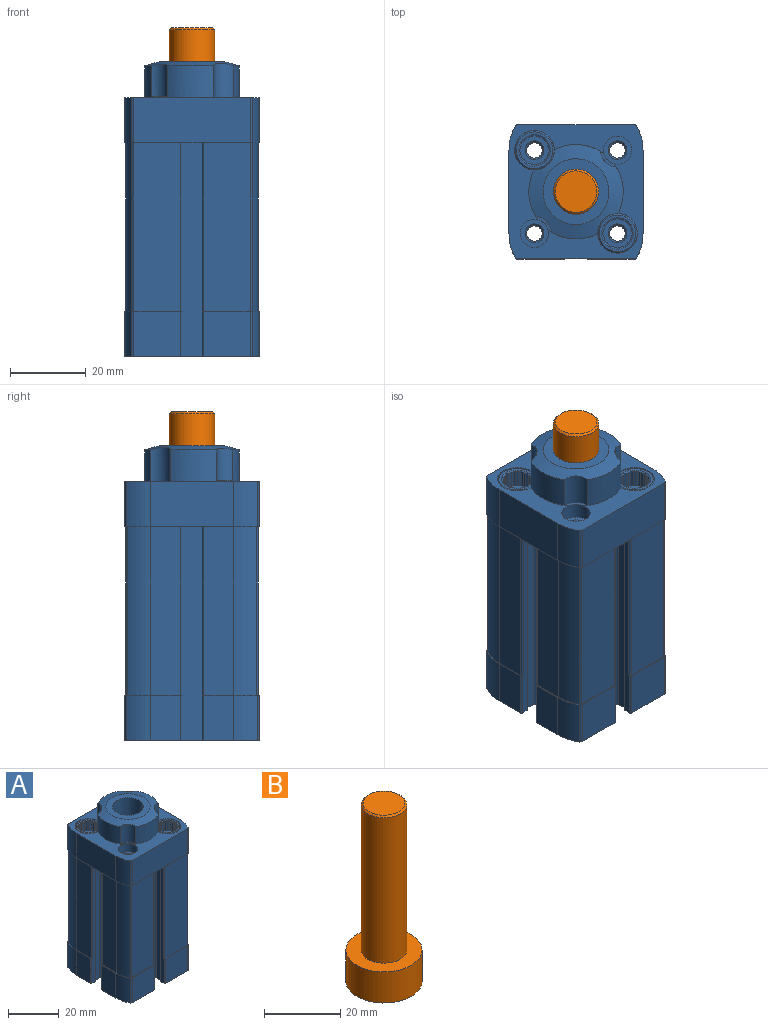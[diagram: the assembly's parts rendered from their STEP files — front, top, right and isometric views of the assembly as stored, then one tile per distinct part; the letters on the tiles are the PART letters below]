
ASSEMBLY  parts=2 mates=1
PART A: 305 faces, bbox 35.5x35.5x78 mm
  f0: cylinder r=4.5mm len=8.67mm, axis (0,0,-1), area 54.5mm2, adj f1,f4,f93,f202
  f1: cylinder r=12.5mm len=13.11mm, axis (0,0,1), area 107.9mm2, adj f0,f93,f186,f196,f201,f202
  f2: cylinder r=12.5mm len=13.11mm, axis (0,0,1), area 107.9mm2, adj f194,f195,f196,f201,f202,f293
  f3: cylinder r=3.75mm len=4.54mm, axis (0,0,1), area 3.6mm2, adj f11,f12,f192,f286
  f4: cylinder r=12.5mm len=13.11mm, axis (0,0,1), area 107.9mm2, adj f0,f93,f179,f186,f201,f202
  f5: cylinder r=3.75mm len=4.54mm, axis (0,0,1), area 3.6mm2, adj f8,f64,f225,f298
  f6: cylinder r=3.75mm len=4.54mm, axis (0,0,1), area 3.6mm2, adj f8,f80,f81,f298
  f7: cylinder r=3.75mm len=4.54mm, axis (0,0,1), area 3.6mm2, adj f8,f65,f66,f298
  f8: cone r=866.03mm half-angle=60deg, axis (0,0,-1), area 10.5mm2, adj f5,f6,f7,f9,f64,f65,f66,f67
  f9: cylinder r=3.75mm len=4.54mm, axis (0,0,1), area 3.6mm2, adj f8,f67,f220,f298
  f10: plane 4.75x0.71mm, normal (1,0,0), area 3.1mm2, adj f11,f192,f217,f286
  f11: plane 4.74x0.62mm, normal (0.5,-0.87,0), area 3.1mm2, adj f3,f10,f192,f286
  f12: plane 4.74x0.62mm, normal (0.87,-0.5,0), area 3.1mm2, adj f3,f192,f250,f286
  f13: plane 4.74x0.62mm, normal (0.5,-0.87,0), area 3.1mm2, adj f14,f192,f285,f286
  f14: plane 4.74x0.62mm, normal (-0.5,-0.87,0), area 3.1mm2, adj f13,f192,f193,f286
  f15: plane 4.75x0.71mm, normal (0,-1,0), area 3.1mm2, adj f192,f193,f249,f286
  f16: plane 4.74x0.62mm, normal (-0.5,-0.87,0), area 3.1mm2, adj f17,f192,f278,f286
  f17: plane 4.75x0.71mm, normal (-1,0,0), area 3.1mm2, adj f16,f192,f277,f286
  f18: plane 4.74x0.62mm, normal (-0.87,-0.5,0), area 3.1mm2, adj f192,f248,f277,f286
  f19: plane 4.74x0.71mm, normal (-1,0,0), area 3.1mm2, adj f20,f192,f279,f286
  f20: plane 4.74x0.62mm, normal (-0.5,0.87,0), area 3.1mm2, adj f19,f192,f280,f286
  f21: plane 4.74x0.62mm, normal (-0.87,0.5,0), area 3.1mm2, adj f192,f247,f280,f286
  f22: plane 4.74x0.62mm, normal (-0.5,0.87,0), area 3.1mm2, adj f23,f192,f284,f286
  f23: plane 4.74x0.62mm, normal (0.5,0.87,0), area 3.1mm2, adj f22,f192,f283,f286
  f24: plane 4.74x0.71mm, normal (0,1,0), area 3.1mm2, adj f192,f246,f283,f286
  f25: plane 4.74x0.62mm, normal (0.5,0.87,0), area 3.1mm2, adj f26,f192,f282,f286
  f26: plane 4.74x0.71mm, normal (1,0,0), area 3.1mm2, adj f25,f192,f281,f286
  f27: plane 4.74x0.62mm, normal (0.87,0.5,0), area 3.1mm2, adj f192,f245,f281,f286
  f28: plane 4.75x0.71mm, normal (1,0,0), area 3.1mm2, adj f29,f198,f215,f254
  f29: plane 4.74x0.62mm, normal (0.5,-0.87,0), area 3.1mm2, adj f28,f198,f216,f254
  f30: plane 4.74x0.62mm, normal (0.87,-0.5,0), area 3.1mm2, adj f198,f216,f244,f254
  f31: plane 4.74x0.62mm, normal (0.5,-0.87,0), area 3.1mm2, adj f32,f198,f218,f254
  f32: plane 4.74x0.62mm, normal (-0.5,-0.87,0), area 3.1mm2, adj f31,f198,f214,f254
  f33: plane 4.75x0.71mm, normal (0,-1,0), area 3.1mm2, adj f198,f214,f243,f254
  f34: plane 4.74x0.62mm, normal (-0.5,-0.87,0), area 3.1mm2, adj f35,f198,f254,f275
  f35: plane 4.75x0.71mm, normal (-1,0,0), area 3.1mm2, adj f34,f198,f254,f274
  f36: plane 4.74x0.62mm, normal (-0.87,-0.5,0), area 3.1mm2, adj f198,f242,f254,f274
  f37: plane 4.74x0.71mm, normal (-1,0,0), area 3.1mm2, adj f38,f198,f254,f273
  f38: plane 4.74x0.62mm, normal (-0.5,0.87,0), area 3.1mm2, adj f37,f198,f254,f272
  f39: plane 4.74x0.62mm, normal (-0.87,0.5,0), area 3.1mm2, adj f198,f241,f254,f272
  f40: plane 4.74x0.62mm, normal (-0.5,0.87,0), area 3.1mm2, adj f41,f198,f254,f271
  f41: plane 4.74x0.62mm, normal (0.5,0.87,0), area 3.1mm2, adj f40,f198,f254,f270
  f42: plane 4.74x0.71mm, normal (0,1,0), area 3.1mm2, adj f198,f240,f254,f270
  f43: plane 4.74x0.62mm, normal (0.5,0.87,0), area 3.1mm2, adj f44,f198,f254,f269
  f44: plane 4.74x0.71mm, normal (1,0,0), area 3.1mm2, adj f43,f198,f254,f268
  f45: plane 4.74x0.62mm, normal (0.87,0.5,0), area 3.1mm2, adj f198,f239,f254,f268
  f46: plane 4.75x0.71mm, normal (1,0,0), area 3.1mm2, adj f47,f180,f181,f256
  f47: plane 4.74x0.62mm, normal (0.5,-0.87,0), area 3.1mm2, adj f46,f181,f256,f257
  f48: plane 4.74x0.62mm, normal (0.87,-0.5,0), area 3.1mm2, adj f181,f238,f256,f257
  f49: plane 4.74x0.62mm, normal (0.5,-0.87,0), area 3.1mm2, adj f50,f181,f256,f258
  f50: plane 4.74x0.62mm, normal (-0.5,-0.87,0), area 3.1mm2, adj f49,f181,f256,f259
  f51: plane 4.75x0.71mm, normal (0,-1,0), area 3.1mm2, adj f181,f237,f256,f259
  f52: plane 4.74x0.62mm, normal (-0.5,-0.87,0), area 3.1mm2, adj f53,f181,f256,f260
  f53: plane 4.75x0.71mm, normal (-1,0,0), area 3.1mm2, adj f52,f181,f256,f261
  f54: plane 4.74x0.62mm, normal (-0.87,-0.5,0), area 3.1mm2, adj f181,f236,f256,f261
  f55: plane 4.74x0.71mm, normal (-1,0,0), area 3.1mm2, adj f56,f181,f256,f262
  f56: plane 4.74x0.62mm, normal (-0.5,0.87,0), area 3.1mm2, adj f55,f181,f256,f263
  f57: plane 4.74x0.62mm, normal (-0.87,0.5,0), area 3.1mm2, adj f181,f235,f256,f263
  f58: plane 4.74x0.62mm, normal (-0.5,0.87,0), area 3.1mm2, adj f59,f181,f256,f264
  f59: plane 4.74x0.62mm, normal (0.5,0.87,0), area 3.1mm2, adj f58,f181,f256,f265
  f60: plane 4.74x0.71mm, normal (0,1,0), area 3.1mm2, adj f181,f234,f256,f265
  f61: plane 4.74x0.62mm, normal (0.5,0.87,0), area 3.1mm2, adj f62,f181,f256,f266
  f62: plane 4.74x0.71mm, normal (1,0,0), area 3.1mm2, adj f61,f181,f256,f267
  f63: plane 4.74x0.62mm, normal (0.87,0.5,0), area 3.1mm2, adj f181,f219,f256,f267
  f64: plane 4.75x0.71mm, normal (1,0,0), area 3.1mm2, adj f5,f8,f65,f298
  f65: plane 4.74x0.62mm, normal (0.5,-0.87,0), area 3.1mm2, adj f7,f8,f64,f298
  f66: plane 4.74x0.62mm, normal (0.87,-0.5,0), area 3.1mm2, adj f7,f8,f220,f298
  f67: plane 4.74x0.62mm, normal (0.5,-0.87,0), area 3.1mm2, adj f8,f9,f68,f298
  f68: plane 4.74x0.62mm, normal (-0.5,-0.87,0), area 3.1mm2, adj f8,f67,f233,f298
  f69: plane 4.75x0.71mm, normal (0,-1,0), area 3.1mm2, adj f8,f221,f233,f298
  f70: plane 4.74x0.62mm, normal (-0.5,-0.87,0), area 3.1mm2, adj f8,f71,f232,f298
  f71: plane 4.75x0.71mm, normal (-1,0,0), area 3.1mm2, adj f8,f70,f231,f298
  f72: plane 4.74x0.62mm, normal (-0.87,-0.5,0), area 3.1mm2, adj f8,f222,f231,f298
  f73: plane 4.74x0.71mm, normal (-1,0,0), area 3.1mm2, adj f8,f74,f230,f298
  f74: plane 4.74x0.62mm, normal (-0.5,0.87,0), area 3.1mm2, adj f8,f73,f229,f298
  f75: plane 4.74x0.62mm, normal (-0.87,0.5,0), area 3.1mm2, adj f8,f223,f229,f298
  f76: plane 4.74x0.62mm, normal (-0.5,0.87,0), area 3.1mm2, adj f8,f77,f227,f298
  f77: plane 4.74x0.62mm, normal (0.5,0.87,0), area 3.1mm2, adj f8,f76,f226,f298
  f78: plane 4.74x0.71mm, normal (0,1,0), area 3.1mm2, adj f8,f224,f226,f298
  f79: plane 4.74x0.62mm, normal (0.5,0.87,0), area 3.1mm2, adj f8,f80,f228,f298
  f80: plane 4.74x0.71mm, normal (1,0,0), area 3.1mm2, adj f6,f8,f79,f298
  f81: plane 4.74x0.62mm, normal (0.87,0.5,0), area 3.1mm2, adj f6,f8,f225,f298
  f82: plane 4.13x4.13mm, normal (0,1,0), area 13.4mm2, adj f83
  f83: cylinder r=2.07mm len=6.57mm, axis (0,1,0), area 85.3mm2, adj f82,f84
  f84: cone r=2.5mm half-angle=45deg, axis (0,1,0), area 8.8mm2, adj f83,f204
  f85: plane 4.13x4.13mm, normal (0,1,0), area 13.4mm2, adj f86
  f86: cylinder r=2.07mm len=5.57mm, axis (0,1,0), area 72.3mm2, adj f85,f87
  f87: cone r=2.5mm half-angle=45deg, axis (0,1,0), area 8.8mm2, adj f86,f164
  f88: plane 20x20mm, normal (0,0,1), area 314.2mm2, adj f89
  f89: cylinder r=10mm len=25mm, axis (0,0,1), area 1570.8mm2, adj f88,f90
  f90: plane 20x20mm, normal (0,0,-1), area 201.1mm2, adj f89,f91
  f91: cylinder r=6mm len=31.25mm, axis (0,0,1), area 1178.1mm2, adj f90,f92
  f92: plane 17.45x17.45mm, normal (0,0,1), area 126mm2, adj f91,f202
  f93: plane 4.16x4.16mm, normal (0,0,1), area 4mm2, adj f0,f1,f4,f186
  f94: plane 9x9mm, normal (0,0,-1), area 63.6mm2, adj f95
  f95: cylinder r=4.5mm len=9mm, axis (0,0,1), area 59.4mm2, adj f94,f161
  f96: cylinder r=0.4mm len=12mm, axis (0,0,-1), area 7.5mm2, adj f103,f147,f161,f206
  f97: cylinder r=0.4mm len=12mm, axis (0,0,-1), area 7.5mm2, adj f115,f161,f208,f299
  f98: cylinder r=0.4mm len=12mm, axis (0,0,-1), area 7.5mm2, adj f118,f161,f210,f299
  f99: cylinder r=0.4mm len=12mm, axis (0,0,-1), area 7.5mm2, adj f130,f161,f209,f300
  f100: cylinder r=0.4mm len=12mm, axis (0,0,-1), area 7.5mm2, adj f133,f161,f176,f300
  f101: cylinder r=0.4mm len=12mm, axis (0,0,-1), area 7.5mm2, adj f145,f147,f161,f175
  f102: cylinder r=0.4mm len=44.5mm, axis (0,0,-1), area 28mm2, adj f103,f147,f148,f154
  f103: plane 56.5x1.85mm, normal (0,-1,0), area 93.4mm2, adj f96,f102,f104,f147,f148,f161
  f104: cylinder r=0.2mm len=56.5mm, axis (0,0,-1), area 17.7mm2, adj f103,f105,f148,f161
  f105: plane 56.5x0.2mm, normal (-1,0,0), area 11.3mm2, adj f104,f106,f148,f161
  f106: cylinder r=0.3mm len=56.5mm, axis (0,0,-1), area 26.6mm2, adj f105,f107,f148,f161
  f107: plane 56.5x2.5mm, normal (0,-1,0), area 141.2mm2, adj f106,f108,f148,f161
  f108: cylinder r=0.6mm len=56.5mm, axis (0,0,-1), area 53.2mm2, adj f107,f109,f148,f161
  f109: plane 56.5x5.6mm, normal (1,0,0), area 316.4mm2, adj f108,f110,f148,f161
  f110: cylinder r=0.6mm len=56.5mm, axis (0,0,-1), area 53.2mm2, adj f109,f111,f148,f161
  f111: plane 56.5x2.5mm, normal (0,1,0), area 141.2mm2, adj f110,f112,f148,f161
  f112: cylinder r=0.3mm len=56.5mm, axis (0,0,-1), area 26.6mm2, adj f111,f113,f148,f161
  f113: plane 56.5x0.2mm, normal (-1,0,0), area 11.3mm2, adj f112,f114,f148,f161
  f114: cylinder r=0.2mm len=56.5mm, axis (0,0,-1), area 17.7mm2, adj f113,f115,f148,f161
  f115: plane 56.5x1.85mm, normal (0,1,0), area 93.4mm2, adj f97,f114,f116,f148,f161,f299
  f116: cylinder r=0.4mm len=44.5mm, axis (0,0,-1), area 28mm2, adj f115,f148,f299,f301
  f117: cylinder r=0.4mm len=44.5mm, axis (0,0,-1), area 28mm2, adj f118,f148,f157,f299
  f118: plane 56.5x1.85mm, normal (-1,0,0), area 93.4mm2, adj f98,f117,f119,f148,f161,f299
  f119: cylinder r=0.2mm len=56.5mm, axis (0,0,-1), area 17.7mm2, adj f118,f120,f148,f161
  f120: plane 56.5x0.2mm, normal (0,1,0), area 11.3mm2, adj f119,f121,f148,f161
  f121: cylinder r=0.3mm len=56.5mm, axis (0,0,-1), area 26.6mm2, adj f120,f122,f148,f161
  f122: plane 56.5x2.5mm, normal (-1,0,0), area 141.2mm2, adj f121,f123,f148,f161
  f123: cylinder r=0.6mm len=56.5mm, axis (0,0,-1), area 53.2mm2, adj f122,f124,f148,f161
  f124: plane 56.5x5.6mm, normal (0,-1,0), area 316.4mm2, adj f123,f125,f148,f161
  f125: cylinder r=0.6mm len=56.5mm, axis (0,0,-1), area 53.2mm2, adj f124,f126,f148,f161
  f126: plane 56.5x2.5mm, normal (1,0,0), area 141.2mm2, adj f125,f127,f148,f161
  f127: cylinder r=0.3mm len=56.5mm, axis (0,0,-1), area 26.6mm2, adj f126,f128,f148,f161
  f128: plane 56.5x0.2mm, normal (0,1,0), area 11.3mm2, adj f127,f129,f148,f161
  f129: cylinder r=0.2mm len=56.5mm, axis (0,0,-1), area 17.7mm2, adj f128,f130,f148,f161
  f130: plane 56.5x1.85mm, normal (1,0,0), area 93.4mm2, adj f99,f129,f131,f148,f161,f300
  f131: cylinder r=0.4mm len=44.5mm, axis (0,0,-1), area 28mm2, adj f130,f148,f300,f302
  f132: cylinder r=0.4mm len=44.5mm, axis (0,0,-1), area 28mm2, adj f133,f148,f160,f300
  f133: plane 56.5x1.85mm, normal (0,1,0), area 93.4mm2, adj f100,f132,f134,f148,f161,f300
  f134: cylinder r=0.2mm len=56.5mm, axis (0,0,-1), area 17.7mm2, adj f133,f135,f148,f161
  f135: plane 56.5x0.2mm, normal (1,0,0), area 11.3mm2, adj f134,f136,f148,f161
  f136: cylinder r=0.3mm len=56.5mm, axis (0,0,-1), area 26.6mm2, adj f135,f137,f148,f161
  f137: plane 56.5x2.5mm, normal (0,1,0), area 141.2mm2, adj f136,f138,f148,f161
  f138: cylinder r=0.6mm len=56.5mm, axis (0,0,-1), area 53.2mm2, adj f137,f139,f148,f161
  f139: plane 56.5x5.6mm, normal (-1,0,0), area 316.4mm2, adj f138,f140,f148,f161
  f140: cylinder r=0.6mm len=56.5mm, axis (0,0,-1), area 53.2mm2, adj f139,f141,f148,f161
  f141: plane 56.5x2.5mm, normal (0,-1,0), area 141.2mm2, adj f140,f142,f148,f161
  f142: cylinder r=0.3mm len=56.5mm, axis (0,0,-1), area 26.6mm2, adj f141,f143,f148,f161
  f143: plane 56.5x0.2mm, normal (1,0,0), area 11.3mm2, adj f142,f144,f148,f161
  f144: cylinder r=0.2mm len=56.5mm, axis (0,0,-1), area 17.7mm2, adj f143,f145,f148,f161
  f145: plane 56.5x1.85mm, normal (0,-1,0), area 93.4mm2, adj f101,f144,f146,f147,f148,f161
  f146: cylinder r=0.4mm len=44.5mm, axis (0,0,-1), area 28mm2, adj f145,f147,f148,f303
  f147: plane 35.5x15.05mm, normal (0,0,1), area 15.5mm2, adj f96,f101,f102,f103,f145,f146,f149,f150
  f148: plane 35.5x35.5mm, normal (0,0,-1), area 138.3mm2, adj f102,f103,f104,f105,f106,f107,f108,f109
  f149: cylinder r=12.75mm len=44.5mm, axis (0,0,-1), area 287.7mm2, adj f147,f148,f150,f303
  f150: cylinder r=0.6mm len=44.5mm, axis (0,0,-1), area 28.4mm2, adj f147,f148,f149,f151
  f151: plane 44.5x30.74mm, normal (0,1,0), area 1368mm2, adj f147,f148,f150,f152
  f152: cylinder r=0.6mm len=44.5mm, axis (0,0,-1), area 28.4mm2, adj f147,f148,f151,f153
  f153: cylinder r=12.75mm len=44.5mm, axis (0,0,-1), area 287.7mm2, adj f147,f148,f152,f154
  f154: plane 44.5x7.9mm, normal (1,0,0), area 351.5mm2, adj f102,f147,f148,f153
  f155: cylinder r=12.75mm len=44.5mm, axis (0,0,-1), area 287.7mm2, adj f148,f156,f299,f301
  f156: cylinder r=0.6mm len=44.5mm, axis (0,0,-1), area 28.4mm2, adj f148,f155,f157,f299
  f157: plane 44.5x12.27mm, normal (0,-1,0), area 546.1mm2, adj f117,f148,f156,f299
  f158: cylinder r=0.6mm len=44.5mm, axis (0,0,-1), area 28.4mm2, adj f148,f159,f300,f302
  f159: cylinder r=12.75mm len=44.5mm, axis (0,0,-1), area 287.7mm2, adj f148,f158,f160,f300
  f160: plane 44.5x7.9mm, normal (-1,0,0), area 351.5mm2, adj f132,f148,f159,f300
  f161: plane 35.5x35.5mm, normal (0,0,-1), area 770.9mm2, adj f95,f96,f97,f98,f99,f100,f101,f103
  f162: plane 9.7x9.7mm, normal (0,0,1), area 18.5mm2, adj f286,f287
  f163: cylinder r=0.85mm len=12mm, axis (0,0,-1), area 10.9mm2, adj f148,f164,f174,f201
  f164: plane 30.74x12mm, normal (0,1,0), area 349.3mm2, adj f87,f148,f163,f165,f201
  f165: cylinder r=0.85mm len=12mm, axis (0,0,-1), area 10.9mm2, adj f148,f164,f166,f201
  f166: cylinder r=13mm len=12mm, axis (0,0,-1), area 79.1mm2, adj f148,f165,f167,f201
  f167: plane 22x12mm, normal (1,0,0), area 264mm2, adj f148,f166,f168,f201
  f168: cylinder r=13mm len=12mm, axis (0,0,-1), area 79.1mm2, adj f148,f167,f169,f201
  f169: cylinder r=0.85mm len=12mm, axis (0,0,-1), area 10.9mm2, adj f148,f168,f170,f201
  f170: plane 30.74x12mm, normal (0,-1,0), area 368.9mm2, adj f148,f169,f171,f201
  f171: cylinder r=0.85mm len=12mm, axis (0,0,-1), area 10.9mm2, adj f148,f170,f172,f201
  f172: cylinder r=13mm len=12mm, axis (0,0,-1), area 79.1mm2, adj f148,f171,f173,f201
  f173: plane 22x12mm, normal (-1,0,0), area 264mm2, adj f148,f172,f174,f201
  f174: cylinder r=13mm len=12mm, axis (0,0,-1), area 79.1mm2, adj f148,f163,f173,f201
  f175: plane 12x7.9mm, normal (-1,0,0), area 94.8mm2, adj f101,f147,f161,f178
  f176: plane 12x7.9mm, normal (-1,0,0), area 94.8mm2, adj f100,f161,f177,f300
  f177: cylinder r=13mm len=12mm, axis (0,0,-1), area 79.1mm2, adj f161,f176,f212,f300
  f178: cylinder r=13mm len=12mm, axis (0,0,-1), area 79.1mm2, adj f147,f161,f175,f304
  f179: cylinder r=5.25mm len=10.5mm, axis (0,0,1), area 88mm2, adj f4,f201,f202,f213,f287
  f180: cylinder r=3.75mm len=4.54mm, axis (0,0,1), area 3.6mm2, adj f46,f181,f219,f256
  f181: plane 8.08x8.08mm, normal (0,0,-1), area 26.5mm2, adj f46,f47,f48,f49,f50,f51,f52,f53
  f182: cone r=2.07mm half-angle=45deg, axis (0,0,-1), area 8.8mm2, adj f181,f183
  f183: cylinder r=2.07mm len=58.83mm, axis (0,0,1), area 764.1mm2, adj f182,f184
  f184: cone r=2.5mm half-angle=45deg, axis (0,0,1), area 8.8mm2, adj f183,f185
  f185: plane 7.5x7.5mm, normal (0,0,1), area 24.5mm2, adj f184,f186
  f186: cylinder r=3.75mm len=7.5mm, axis (0,0,1), area 95.1mm2, adj f1,f4,f93,f185,f201
  f187: cylinder r=4.5mm len=9mm, axis (0,0,1), area 135.7mm2, adj f161,f188
  f188: plane 9x9mm, normal (0,0,-1), area 44mm2, adj f187,f189
  f189: cone r=2.07mm half-angle=45deg, axis (0,0,-1), area 8.8mm2, adj f188,f190
  f190: cylinder r=2.07mm len=58.03mm, axis (0,0,1), area 753.7mm2, adj f189,f191
  f191: cone r=2.5mm half-angle=45deg, axis (0,0,1), area 8.8mm2, adj f190,f192
  f192: plane 8.08x8.08mm, normal (0,0,1), area 26.5mm2, adj f3,f10,f11,f12,f13,f14,f15,f16
  f193: cylinder r=3.75mm len=4.54mm, axis (0,0,1), area 3.6mm2, adj f14,f15,f192,f286
  f194: plane 4.16x4.16mm, normal (0,0,1), area 4mm2, adj f2,f195,f213,f293
  f195: cylinder r=4.5mm len=8.67mm, axis (0,0,-1), area 54.5mm2, adj f2,f194,f202,f213
  f196: cylinder r=5.25mm len=10.5mm, axis (0,0,1), area 88mm2, adj f1,f2,f197,f201,f202
  f197: cone r=5.25mm half-angle=45deg, axis (0,0,-1), area 17.9mm2, adj f196,f199
  f198: cone r=4.2mm half-angle=60deg, axis (0,0,1), area 10.5mm2, adj f28,f29,f30,f31,f32,f33,f34,f35
  f199: plane 9.7x9.7mm, normal (0,0,1), area 18.5mm2, adj f197,f198
  f200: cylinder r=5.25mm len=10.5mm, axis (0,0,1), area 13.2mm2, adj f161,f252
  f201: plane 35.5x35.5mm, normal (0,0,1), area 517.6mm2, adj f1,f2,f4,f163,f164,f165,f166,f167
  f202: sphere r=38mm, area 226.6mm2, adj f0,f1,f2,f4,f92,f179,f195,f196
  f203: cylinder r=0.85mm len=12mm, axis (0,0,-1), area 10.9mm2, adj f147,f161,f204,f205
  f204: plane 30.74x12mm, normal (0,1,0), area 349.3mm2, adj f84,f147,f161,f203,f304
  f205: cylinder r=13mm len=12mm, axis (0,0,-1), area 79.1mm2, adj f147,f161,f203,f206
  f206: plane 12x7.9mm, normal (1,0,0), area 94.8mm2, adj f96,f147,f161,f205
  f207: cylinder r=13mm len=12mm, axis (0,0,-1), area 79.1mm2, adj f161,f208,f211,f299
  f208: plane 12x7.9mm, normal (1,0,0), area 94.8mm2, adj f97,f161,f207,f299
  f209: plane 12.27x12mm, normal (0,-1,0), area 147.3mm2, adj f99,f161,f212,f300
  f210: plane 12.27x12mm, normal (0,-1,0), area 147.3mm2, adj f98,f161,f211,f299
  f211: cylinder r=0.85mm len=12mm, axis (0,0,-1), area 10.9mm2, adj f161,f207,f210,f299
  f212: cylinder r=0.85mm len=12mm, axis (0,0,-1), area 10.9mm2, adj f161,f177,f209,f300
  f213: cylinder r=12.5mm len=13.11mm, axis (0,0,1), area 107.9mm2, adj f179,f194,f195,f201,f202,f293
  f214: cylinder r=3.75mm len=4.54mm, axis (0,0,1), area 3.6mm2, adj f32,f33,f198,f254
  f215: cylinder r=3.75mm len=4.54mm, axis (0,0,1), area 3.6mm2, adj f28,f198,f239,f254
  f216: cylinder r=3.75mm len=4.54mm, axis (0,0,1), area 3.6mm2, adj f29,f30,f198,f254
  f217: cylinder r=3.75mm len=4.54mm, axis (0,0,1), area 3.6mm2, adj f10,f192,f245,f286
  f218: cylinder r=3.75mm len=4.54mm, axis (0,0,1), area 3.6mm2, adj f31,f198,f244,f254
  f219: plane 4.74x0.62mm, normal (0.87,-0.5,0), area 3.1mm2, adj f63,f180,f181,f256
  f220: plane 4.74x0.71mm, normal (0,-1,0), area 3.1mm2, adj f8,f9,f66,f298
  f221: plane 4.74x0.62mm, normal (-0.87,-0.5,0), area 3.1mm2, adj f8,f69,f232,f298
  f222: plane 4.74x0.62mm, normal (-0.87,0.5,0), area 3.1mm2, adj f8,f72,f230,f298
  f223: plane 4.75x0.71mm, normal (0,1,0), area 3.1mm2, adj f8,f75,f227,f298
  f224: plane 4.74x0.62mm, normal (0.87,0.5,0), area 3.1mm2, adj f8,f78,f228,f298
  f225: plane 4.74x0.62mm, normal (0.87,-0.5,0), area 3.1mm2, adj f5,f8,f81,f298
  f226: cylinder r=3.75mm len=4.54mm, axis (0,0,1), area 3.6mm2, adj f8,f77,f78,f298
  f227: cylinder r=3.75mm len=4.54mm, axis (0,0,1), area 3.6mm2, adj f8,f76,f223,f298
  f228: cylinder r=3.75mm len=4.54mm, axis (0,0,1), area 3.6mm2, adj f8,f79,f224,f298
  f229: cylinder r=3.75mm len=4.54mm, axis (0,0,1), area 3.6mm2, adj f8,f74,f75,f298
  f230: cylinder r=3.75mm len=4.54mm, axis (0,0,1), area 3.6mm2, adj f8,f73,f222,f298
  f231: cylinder r=3.75mm len=4.54mm, axis (0,0,1), area 3.6mm2, adj f8,f71,f72,f298
  f232: cylinder r=3.75mm len=4.54mm, axis (0,0,1), area 3.6mm2, adj f8,f70,f221,f298
  f233: cylinder r=3.75mm len=4.54mm, axis (0,0,1), area 3.6mm2, adj f8,f68,f69,f298
  f234: plane 4.74x0.62mm, normal (0.87,0.5,0), area 3.1mm2, adj f60,f181,f256,f266
  f235: plane 4.75x0.71mm, normal (0,1,0), area 3.1mm2, adj f57,f181,f256,f264
  f236: plane 4.74x0.62mm, normal (-0.87,0.5,0), area 3.1mm2, adj f54,f181,f256,f262
  f237: plane 4.74x0.62mm, normal (-0.87,-0.5,0), area 3.1mm2, adj f51,f181,f256,f260
  f238: plane 4.74x0.71mm, normal (0,-1,0), area 3.1mm2, adj f48,f181,f256,f258
  f239: plane 4.74x0.62mm, normal (0.87,-0.5,0), area 3.1mm2, adj f45,f198,f215,f254
  f240: plane 4.74x0.62mm, normal (0.87,0.5,0), area 3.1mm2, adj f42,f198,f254,f269
  f241: plane 4.75x0.71mm, normal (0,1,0), area 3.1mm2, adj f39,f198,f254,f271
  f242: plane 4.74x0.62mm, normal (-0.87,0.5,0), area 3.1mm2, adj f36,f198,f254,f273
  f243: plane 4.74x0.62mm, normal (-0.87,-0.5,0), area 3.1mm2, adj f33,f198,f254,f275
  f244: plane 4.74x0.71mm, normal (0,-1,0), area 3.1mm2, adj f30,f198,f218,f254
  f245: plane 4.74x0.62mm, normal (0.87,-0.5,0), area 3.1mm2, adj f27,f192,f217,f286
  f246: plane 4.74x0.62mm, normal (0.87,0.5,0), area 3.1mm2, adj f24,f192,f282,f286
  f247: plane 4.75x0.71mm, normal (0,1,0), area 3.1mm2, adj f21,f192,f284,f286
  f248: plane 4.74x0.62mm, normal (-0.87,0.5,0), area 3.1mm2, adj f18,f192,f279,f286
  f249: plane 4.74x0.62mm, normal (-0.87,-0.5,0), area 3.1mm2, adj f15,f192,f278,f286
  f250: plane 4.74x0.71mm, normal (0,-1,0), area 3.1mm2, adj f12,f192,f285,f286
  f251: plane 9.7x9.7mm, normal (0,0,-1), area 18.5mm2, adj f8,f252
  f252: cone r=4.85mm half-angle=45deg, axis (0,0,1), area 17.9mm2, adj f200,f251
  f253: plane 9.7x9.7mm, normal (0,0,-1), area 18.5mm2, adj f255,f256
  f254: plane 8.08x8.08mm, normal (0,0,1), area 26.5mm2, adj f28,f29,f30,f31,f32,f33,f34,f35
  f255: cone r=4.85mm half-angle=45deg, axis (0,0,1), area 17.9mm2, adj f253,f276
  f256: cone r=866.03mm half-angle=60deg, axis (0,0,-1), area 10.5mm2, adj f46,f47,f48,f49,f50,f51,f52,f53
  f257: cylinder r=3.75mm len=4.54mm, axis (0,0,1), area 3.6mm2, adj f47,f48,f181,f256
  f258: cylinder r=3.75mm len=4.54mm, axis (0,0,1), area 3.6mm2, adj f49,f181,f238,f256
  f259: cylinder r=3.75mm len=4.54mm, axis (0,0,1), area 3.6mm2, adj f50,f51,f181,f256
  f260: cylinder r=3.75mm len=4.54mm, axis (0,0,1), area 3.6mm2, adj f52,f181,f237,f256
  f261: cylinder r=3.75mm len=4.54mm, axis (0,0,1), area 3.6mm2, adj f53,f54,f181,f256
  f262: cylinder r=3.75mm len=4.54mm, axis (0,0,1), area 3.6mm2, adj f55,f181,f236,f256
  f263: cylinder r=3.75mm len=4.54mm, axis (0,0,1), area 3.6mm2, adj f56,f57,f181,f256
  f264: cylinder r=3.75mm len=4.54mm, axis (0,0,1), area 3.6mm2, adj f58,f181,f235,f256
  f265: cylinder r=3.75mm len=4.54mm, axis (0,0,1), area 3.6mm2, adj f59,f60,f181,f256
  f266: cylinder r=3.75mm len=4.54mm, axis (0,0,1), area 3.6mm2, adj f61,f181,f234,f256
  f267: cylinder r=3.75mm len=4.54mm, axis (0,0,1), area 3.6mm2, adj f62,f63,f181,f256
  f268: cylinder r=3.75mm len=4.54mm, axis (0,0,1), area 3.6mm2, adj f44,f45,f198,f254
  f269: cylinder r=3.75mm len=4.54mm, axis (0,0,1), area 3.6mm2, adj f43,f198,f240,f254
  f270: cylinder r=3.75mm len=4.54mm, axis (0,0,1), area 3.6mm2, adj f41,f42,f198,f254
  f271: cylinder r=3.75mm len=4.54mm, axis (0,0,1), area 3.6mm2, adj f40,f198,f241,f254
  f272: cylinder r=3.75mm len=4.54mm, axis (0,0,1), area 3.6mm2, adj f38,f39,f198,f254
  f273: cylinder r=3.75mm len=4.54mm, axis (0,0,1), area 3.6mm2, adj f37,f198,f242,f254
  f274: cylinder r=3.75mm len=4.54mm, axis (0,0,1), area 3.6mm2, adj f35,f36,f198,f254
  f275: cylinder r=3.75mm len=4.54mm, axis (0,0,1), area 3.6mm2, adj f34,f198,f243,f254
  f276: cylinder r=5.25mm len=10.5mm, axis (0,0,1), area 13.2mm2, adj f161,f255
  f277: cylinder r=3.75mm len=4.54mm, axis (0,0,1), area 3.6mm2, adj f17,f18,f192,f286
  f278: cylinder r=3.75mm len=4.54mm, axis (0,0,1), area 3.6mm2, adj f16,f192,f249,f286
  f279: cylinder r=3.75mm len=4.54mm, axis (0,0,1), area 3.6mm2, adj f19,f192,f248,f286
  f280: cylinder r=3.75mm len=4.54mm, axis (0,0,1), area 3.6mm2, adj f20,f21,f192,f286
  f281: cylinder r=3.75mm len=4.54mm, axis (0,0,1), area 3.6mm2, adj f26,f27,f192,f286
  f282: cylinder r=3.75mm len=4.54mm, axis (0,0,1), area 3.6mm2, adj f25,f192,f246,f286
  f283: cylinder r=3.75mm len=4.54mm, axis (0,0,1), area 3.6mm2, adj f23,f24,f192,f286
  f284: cylinder r=3.75mm len=4.54mm, axis (0,0,1), area 3.6mm2, adj f22,f192,f247,f286
  f285: cylinder r=3.75mm len=4.54mm, axis (0,0,1), area 3.6mm2, adj f13,f192,f250,f286
  f286: cone r=4.2mm half-angle=60deg, axis (0,0,1), area 10.5mm2, adj f3,f10,f11,f12,f13,f14,f15,f16
  f287: cone r=5.25mm half-angle=45deg, axis (0,0,-1), area 17.9mm2, adj f162,f179
  f288: cone r=2.5mm half-angle=45deg, axis (0,0,1), area 8.8mm2, adj f254,f289
  f289: cylinder r=2.07mm len=58.03mm, axis (0,0,1), area 753.7mm2, adj f288,f290
  f290: cone r=2.07mm half-angle=45deg, axis (0,0,-1), area 8.8mm2, adj f289,f291
  f291: plane 9x9mm, normal (0,0,-1), area 44mm2, adj f290,f292
  f292: cylinder r=4.5mm len=9mm, axis (0,0,1), area 135.7mm2, adj f161,f291
  f293: cylinder r=3.75mm len=7.5mm, axis (0,0,1), area 95.1mm2, adj f2,f194,f201,f213,f294
  f294: plane 7.5x7.5mm, normal (0,0,1), area 24.5mm2, adj f293,f295
  f295: cone r=2.5mm half-angle=45deg, axis (0,0,1), area 8.8mm2, adj f294,f296
  f296: cylinder r=2.07mm len=58.83mm, axis (0,0,1), area 764.1mm2, adj f295,f297
  f297: cone r=2.07mm half-angle=45deg, axis (0,0,-1), area 8.8mm2, adj f296,f298
  f298: plane 8.08x8.08mm, normal (0,0,-1), area 26.5mm2, adj f5,f6,f7,f9,f64,f65,f66,f67
  f299: plane 15.05x15.05mm, normal (0,0,1), area 7.1mm2, adj f97,f98,f115,f116,f117,f118,f155,f156
  f300: plane 15.05x15.05mm, normal (0,0,1), area 7.1mm2, adj f99,f100,f130,f131,f132,f133,f158,f159
  f301: plane 44.5x7.9mm, normal (1,0,0), area 351.5mm2, adj f116,f148,f155,f299
  f302: plane 44.5x12.27mm, normal (0,-1,0), area 546.1mm2, adj f131,f148,f158,f300
  f303: plane 44.5x7.9mm, normal (-1,0,0), area 351.5mm2, adj f146,f147,f148,f149
  f304: cylinder r=0.85mm len=12mm, axis (0,0,-1), area 10.9mm2, adj f147,f161,f178,f204
PART B: 6 faces, bbox 20x20x57.3 mm
  f0: cylinder r=10mm len=20mm, axis (0,0,1), area 628.3mm2, adj f1,f5
  f1: plane 20x20mm, normal (0,0,1), area 201.1mm2, adj f0,f2
  f2: cylinder r=6mm len=46.75mm, axis (0,0,1), area 1762.4mm2, adj f1,f3
  f3: cone r=5.5mm half-angle=45deg, axis (0,0,-1), area 25.5mm2, adj f2,f4
  f4: plane 11x11mm, normal (0,0,1), area 95mm2, adj f3
  f5: plane 20x20mm, normal (0,0,-1), area 314.2mm2, adj f0
PLACE A t=(-4.01,1.29,8.37)mm
PLACE B t=(-4.01,1.29,15.91)mm
MATE slider B.f0 <-> A.f1  axis (0,0,1) through (-4.01,1.29,-30.34)mm
